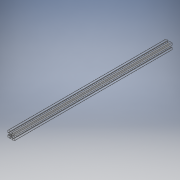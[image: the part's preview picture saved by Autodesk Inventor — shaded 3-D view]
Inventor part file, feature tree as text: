
AUTODESK INVENTOR PART (.ipt)
format: ipt  version: 2019 (Build 230136000, 136)  size: 232,960 bytes
history: native  units: in
note: dims shown in document units (in); Inventor stores cm internally (conversion verified against a paired STEP export)
features: plane x1, extrude x1, sketch x1
ambient origin geometry x8: Origin, YZ Plane, XZ Plane, XY Plane, X Axis, Y Axis, Z Axis, Center Point
bodies: Solid1 (feature_tree)
feature tree (3):
  plane  "Work Plane1"
  extrude  "Extrusion1"  [1 undecoded]
  sketch  "Sketch1"  dims[d0=36.0in d1=0.0in]
note: 1 required parameter value undecoded (feature->parameter linkage not recoverable at this tier; creation-order binding heuristic only, values carry confidence <= 0.55)
